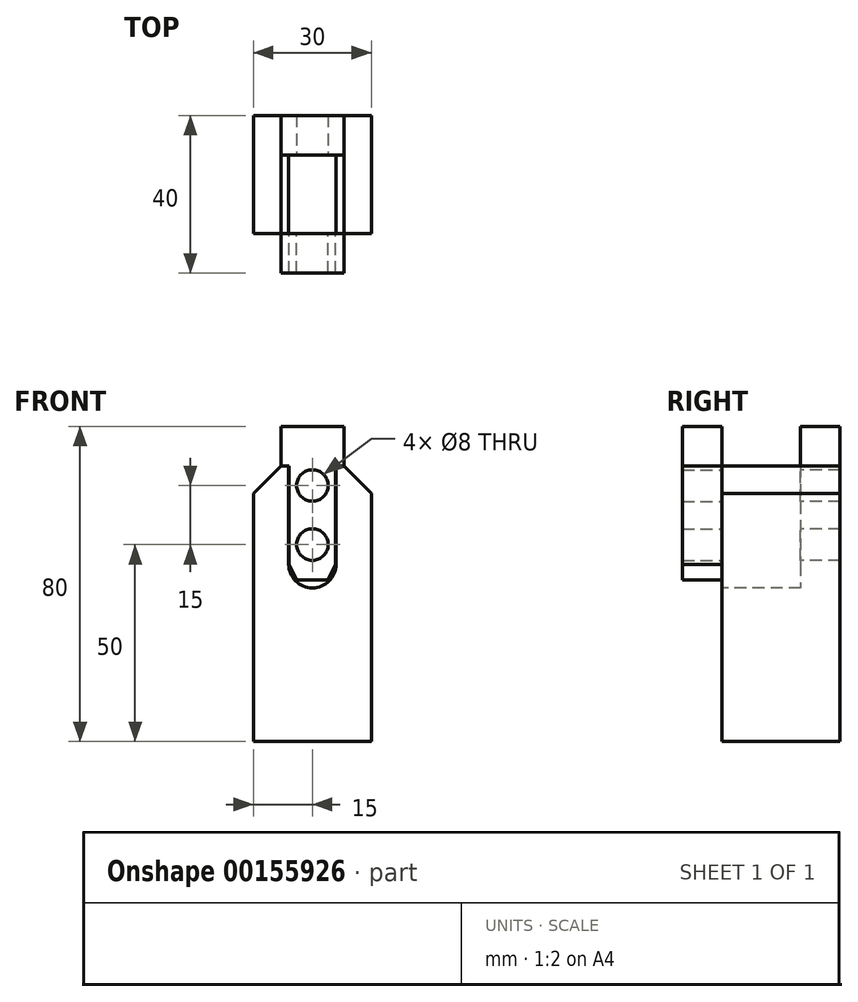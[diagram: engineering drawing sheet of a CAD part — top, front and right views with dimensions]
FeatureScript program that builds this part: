
annotation { "Feature Type Name" : "Feature", "Feature Type Description" : "" }
export const myFeature = defineFeature(function(context is Context, id is Id, definition is map)
    precondition{}
    {
        {
            var Q0;
            Q0=qCreatedBy(makeId("Top.planeOp"),FACE);
            var sketch = newSketch(context, id + "F0", { "sketchPlane" : qUnion([Q0])});
            skLineSegment(sketch, "E0.bottom", {"start": v(15, 15) * mm, "end": v(-15, 15) * mm});
            skLineSegment(sketch, "E0.top", {"start": v(15, -15) * mm, "end": v(-15, -15) * mm});
            skLineSegment(sketch, "E0.left", {"start": v(15, 15) * mm, "end": v(15, -15) * mm});
            skLineSegment(sketch, "E0.right", {"start": v(-15, 15) * mm, "end": v(-15, -15) * mm});
            skPoint(sketch, "E0.middle", {"position": v(0, 0) * mm});
            skSolve(sketch);
        }
        {
            var Q0;
            Q0 = qSketchRegion(id + "F0", true);
            extrude(context, id + "F1", {"entities" : qUnion([Q0]), "depth" : 80 * mm});
        }
        {
            var Q0;
            Q0=makeQuery(id+"F1.opExtrude","SWEPT_FACE",FACE,{"disambiguationData":[OSD([sQuery(id+"F0.wireOp",EDGE,"E0.left")])]});
            var sketch = newSketch(context, id + "F2", { "sketchPlane" : qUnion([Q0])});
            skLineSegment(sketch, "E1.bottom", {"start": v(-15, 80) * mm, "end": v(5, 80) * mm});
            skLineSegment(sketch, "E1.top", {"start": v(-15, 70) * mm, "end": v(5, 70) * mm});
            skLineSegment(sketch, "E1.left", {"start": v(-15, 80) * mm, "end": v(-15, 70) * mm});
            skLineSegment(sketch, "E1.right", {"start": v(5, 80) * mm, "end": v(5, 70) * mm});
            skSolve(sketch);
        }
        {
            var Q0;
            Q0=makeQuery(id+"F2.imprint","IMPRINT",FACE,{"disambiguationData":[TD([[makeQuery(id+"F2.imprint","IMPRINT",EDGE,{"derivedFrom":sQuery(id+"F2.wireOp",EDGE,"E1.bottom")}),1.0]])]});
            extrude(context, id + "F3", {"entities" : qUnion([Q0]), "operationType" : NewBodyOperationType.REMOVE, "endBound" : BoundingType.THROUGH_ALL, "oppositeDirection" : true, "depth" : 25 * mm});
        }
        {
            var Q0;
            Q0=makeQuery(id+"F1.opExtrude","SWEPT_FACE",FACE,{"disambiguationData":[OSD([sQuery(id+"F0.wireOp",EDGE,"E0.bottom")])]});
            var sketch = newSketch(context, id + "F4", { "sketchPlane" : qUnion([Q0])});
            skLineSegment(sketch, "E2.bottom", {"start": v(-15, 80) * mm, "end": v(-8, 80) * mm});
            skLineSegment(sketch, "E2.top", {"start": v(-15, 70) * mm, "end": v(-8, 70) * mm});
            skLineSegment(sketch, "E2.left", {"start": v(-15, 80) * mm, "end": v(-15, 70) * mm});
            skLineSegment(sketch, "E2.right", {"start": v(-8, 80) * mm, "end": v(-8, 70) * mm});
            skLineSegment(sketch, "E3.MirrorCS", {"start": v(15, 80) * mm, "end": v(15, 70) * mm});
            skLineSegment(sketch, "E4.MirrorCS", {"start": v(15, 80) * mm, "end": v(8, 80) * mm});
            skLineSegment(sketch, "E5.MirrorCS", {"start": v(15, 70) * mm, "end": v(8, 70) * mm});
            skLineSegment(sketch, "E6.MirrorCS", {"start": v(8, 80) * mm, "end": v(8, 70) * mm});
            skSolve(sketch);
        }
        {
            var Q0;
            Q0=makeQuery(id+"F4.imprint","IMPRINT",FACE,{"disambiguationData":[TD([[makeQuery(id+"F4.imprint","IMPRINT",EDGE,{"derivedFrom":sQuery(id+"F4.wireOp",EDGE,"E2.bottom")}),-1.0]])]});
            var Q1;
            Q1=makeQuery(id+"F4.imprint","IMPRINT",FACE,{"disambiguationData":[TD([[makeQuery(id+"F4.imprint","IMPRINT",EDGE,{"derivedFrom":sQuery(id+"F4.wireOp",EDGE,"E3.MirrorCS")}),-1.0]])]});
            extrude(context, id + "F5", {"entities" : qUnion([Q0, Q1]), "operationType" : NewBodyOperationType.REMOVE, "endBound" : BoundingType.THROUGH_ALL, "oppositeDirection" : true, "depth" : 25 * mm});
        }
        {
            var Q0;
            Q0=makeQuery(id+"F1.opExtrude","SWEPT_FACE",FACE,{"disambiguationData":[OSD([sQuery(id+"F0.wireOp",EDGE,"E0.top")])]});
            var sketch = newSketch(context, id + "F6", { "sketchPlane" : qUnion([Q0])});
            skLineSegment(sketch, "E7", {"start": v(-8, 70) * mm, "end": v(-15, 63) * mm});
            skLineSegment(sketch, "E8", {"start": v(-15, 63) * mm, "end": v(-15, 70) * mm});
            skLineSegment(sketch, "E9", {"start": v(-15, 70) * mm, "end": v(-8, 70) * mm});
            skLineSegment(sketch, "E10.MirrorCS", {"start": v(15, 63) * mm, "end": v(15, 70) * mm});
            skLineSegment(sketch, "E11.MirrorCS", {"start": v(15, 70) * mm, "end": v(8, 70) * mm});
            skLineSegment(sketch, "E12.MirrorCS", {"start": v(8, 70) * mm, "end": v(15, 63) * mm});
            skSolve(sketch);
        }
        {
            var Q0;
            Q0=makeQuery(id+"F6.imprint","IMPRINT",FACE,{"disambiguationData":[TD([[makeQuery(id+"F6.imprint","IMPRINT",EDGE,{"derivedFrom":sQuery(id+"F6.wireOp",EDGE,"E10.MirrorCS")}),-1.0]])]});
            var Q1;
            Q1=makeQuery(id+"F6.imprint","IMPRINT",FACE,{"disambiguationData":[TD([[makeQuery(id+"F6.imprint","IMPRINT",EDGE,{"derivedFrom":sQuery(id+"F6.wireOp",EDGE,"E7")}),-1.0]])]});
            extrude(context, id + "F7", {"entities" : qUnion([Q0, Q1]), "operationType" : NewBodyOperationType.REMOVE, "endBound" : BoundingType.THROUGH_ALL, "oppositeDirection" : true, "depth" : 25 * mm});
        }
        {
            var Q0;
            Q0=makeQuery(id+"F1.opExtrude","SWEPT_FACE",FACE,{"disambiguationData":[OSD([sQuery(id+"F0.wireOp",EDGE,"E0.top")])]});
            var sketch = newSketch(context, id + "F8", { "sketchPlane" : qUnion([Q0])});
            skLineSegment(sketch, "E13.bottom", {"start": v(-6, 70) * mm, "end": v(6, 70) * mm});
            skLineSegment(sketch, "E13.top", {"start": v(-6, 45) * mm, "end": v(6, 45) * mm});
            skLineSegment(sketch, "E13.left", {"start": v(-6, 70) * mm, "end": v(-6, 45) * mm});
            skLineSegment(sketch, "E13.right", {"start": v(6, 70) * mm, "end": v(6, 45) * mm});
            skPoint(sketch, "E13.middle", {"position": v(0, 57.5) * mm});
            skPoint(sketch, "E13.middle.positionSnap0", {"position": v(0, 70) * mm});
            skPoint(sketch, "E13.centerSnap0", {"position": v(0, 70) * mm});
            skArc(sketch, "E14", {"start": v(-6, 45) * mm, "mid": v(0, 39) * mm, "end": v(6, 45) * mm});
            skSolve(sketch);
        }
        {
            var Q0;
            Q0=makeQuery(id+"F8.imprint","IMPRINT",FACE,{"disambiguationData":[TD([[makeQuery(id+"F8.imprint","IMPRINT",EDGE,{"derivedFrom":sQuery(id+"F8.wireOp",EDGE,"E13.bottom")}),-1.0]])]});
            var Q1;
            Q1=makeQuery(id+"F8.imprint","IMPRINT",FACE,{"disambiguationData":[TD([[makeQuery(id+"F8.imprint","IMPRINT",EDGE,{"derivedFrom":sQuery(id+"F8.wireOp",EDGE,"E13.top")}),-1.0]])]});
            extrude(context, id + "F9", {"entities" : qUnion([Q0, Q1]), "operationType" : NewBodyOperationType.REMOVE, "oppositeDirection" : true, "depth" : 20 * mm});
        }
        {
            var Q0;
            Q0=makeQuery(id+"F9.boolean.opBoolean","MERGE",FACE,{"derivedFrom":[makeQuery(id+"F3.boolean.opBoolean","COPY",FACE,{"derivedFrom":makeQuery(id+"F3.opExtrude","SWEPT_FACE",FACE,{"disambiguationData":[OSD([sQuery(id+"F2.wireOp",EDGE,"E1.right")])]})}),makeQuery(id+"F9.opExtrude","CAP_FACE",FACE,{"disambiguationData":[OSD([sQuery(id+"F8.wireOp",EDGE,"E13.bottom"),sQuery(id+"F8.wireOp",EDGE,"E13.left"),sQuery(id+"F8.wireOp",EDGE,"E13.right"),sQuery(id+"F8.wireOp",EDGE,"E14")])],"isStart":false})]});
            var sketch = newSketch(context, id + "F10", { "sketchPlane" : qUnion([Q0])});
            skPoint(sketch, "E15", {"position": v(0, 50) * mm});
            skPoint(sketch, "E16", {"position": v(0, 75) * mm});
            skPoint(sketch, "E17", {"position": v(0, 65) * mm});
            skSolve(sketch);
        }
        {
            var Q0;
            Q0=sQuery(id+"F10.wireOp",VERTEX,"E17");
            var Q1;
            Q1=sQuery(id+"F10.wireOp",VERTEX,"E15");
            var Q2;
            Q2=makeQuery(id+"F1.opExtrude","SWEPT_BODY",BODY,{"disambiguationData":[OSD([sQuery(id+"F0.wireOp",EDGE,"E0.bottom"),sQuery(id+"F0.wireOp",EDGE,"E0.top"),sQuery(id+"F0.wireOp",EDGE,"E0.left"),sQuery(id+"F0.wireOp",EDGE,"E0.right")])]});
            hole(context, id + "F11", {"style" : HoleStyle.SIMPLE, "endStyle" : HoleEndStyle.THROUGH, "holeDiameter" : 8 * mm, "startFromSketch" : true, "locations" : qUnion([Q0, Q1]), "scope" : qUnion([Q2]), "tappedDepth" : 12 * mm, "tapClearance" : 3});
        }
        {
            var Q0;
            Q0=makeQuery(id+"F1.opExtrude","SWEPT_FACE",FACE,{"disambiguationData":[OSD([sQuery(id+"F0.wireOp",EDGE,"E0.top")])]});
            var sketch = newSketch(context, id + "F12", { "sketchPlane" : qUnion([Q0])});
            skLineSegment(sketch, "E18.0", {"start": v(-8, 70) * mm, "end": v(-8, 80) * mm});
            skLineSegment(sketch, "E19.0", {"start": v(-8, 80) * mm, "end": v(8, 80) * mm});
            skLineSegment(sketch, "E20.0", {"start": v(8, 70) * mm, "end": v(8, 80) * mm});
            skLineSegment(sketch, "E21", {"start": v(-8, 70) * mm, "end": v(-5.9, 70) * mm});
            skLineSegment(sketch, "E22", {"start": v(-5.9, 70) * mm, "end": v(-5.9, 45) * mm});
            skLineSegment(sketch, "E23", {"start": v(-5.9, 45) * mm, "end": v(5.9, 45) * mm});
            skLineSegment(sketch, "E24", {"start": v(5.9, 45) * mm, "end": v(5.9, 70) * mm});
            skLineSegment(sketch, "E25", {"start": v(5.9, 70) * mm, "end": v(8, 70) * mm});
            skLineSegment(sketch, "E26", {"start": v(-5.9, 45) * mm, "end": v(-4, 41) * mm});
            skLineSegment(sketch, "E27", {"start": v(-4, 41) * mm, "end": v(4, 41) * mm});
            skLineSegment(sketch, "E28", {"start": v(4, 41) * mm, "end": v(5.9, 45) * mm});
            skSolve(sketch);
        }
        {
            var Q0;
            Q0 = qSketchRegion(id + "F12", true);
            extrude(context, id + "F13", {"entities" : qUnion([Q0]), "depth" : 10 * mm});
        }
        {
            var Q0;
            Q0=sQuery(id+"F10.wireOp",VERTEX,"E17");
            var Q1;
            Q1=sQuery(id+"F10.wireOp",VERTEX,"E15");
            var Q2;
            Q2=makeQuery(id+"F13.opExtrude","SWEPT_BODY",BODY,{"disambiguationData":[OSD([sQuery(id+"F12.wireOp",EDGE,"E18.0"),sQuery(id+"F12.wireOp",EDGE,"E19.0"),sQuery(id+"F12.wireOp",EDGE,"E20.0"),sQuery(id+"F12.wireOp",EDGE,"E21"),sQuery(id+"F12.wireOp",EDGE,"E22"),sQuery(id+"F12.wireOp",EDGE,"E24"),sQuery(id+"F12.wireOp",EDGE,"E25"),sQuery(id+"F12.wireOp",EDGE,"E26"),sQuery(id+"F12.wireOp",EDGE,"E27"),sQuery(id+"F12.wireOp",EDGE,"E28")])]});
            hole(context, id + "F14", {"style" : HoleStyle.SIMPLE, "endStyle" : HoleEndStyle.THROUGH, "oppositeDirection" : true, "holeDiameter" : 8 * mm, "startFromSketch" : true, "locations" : qUnion([Q0, Q1]), "scope" : qUnion([Q2]), "tappedDepth" : 12 * mm, "tapClearance" : 3});
        }
    });
